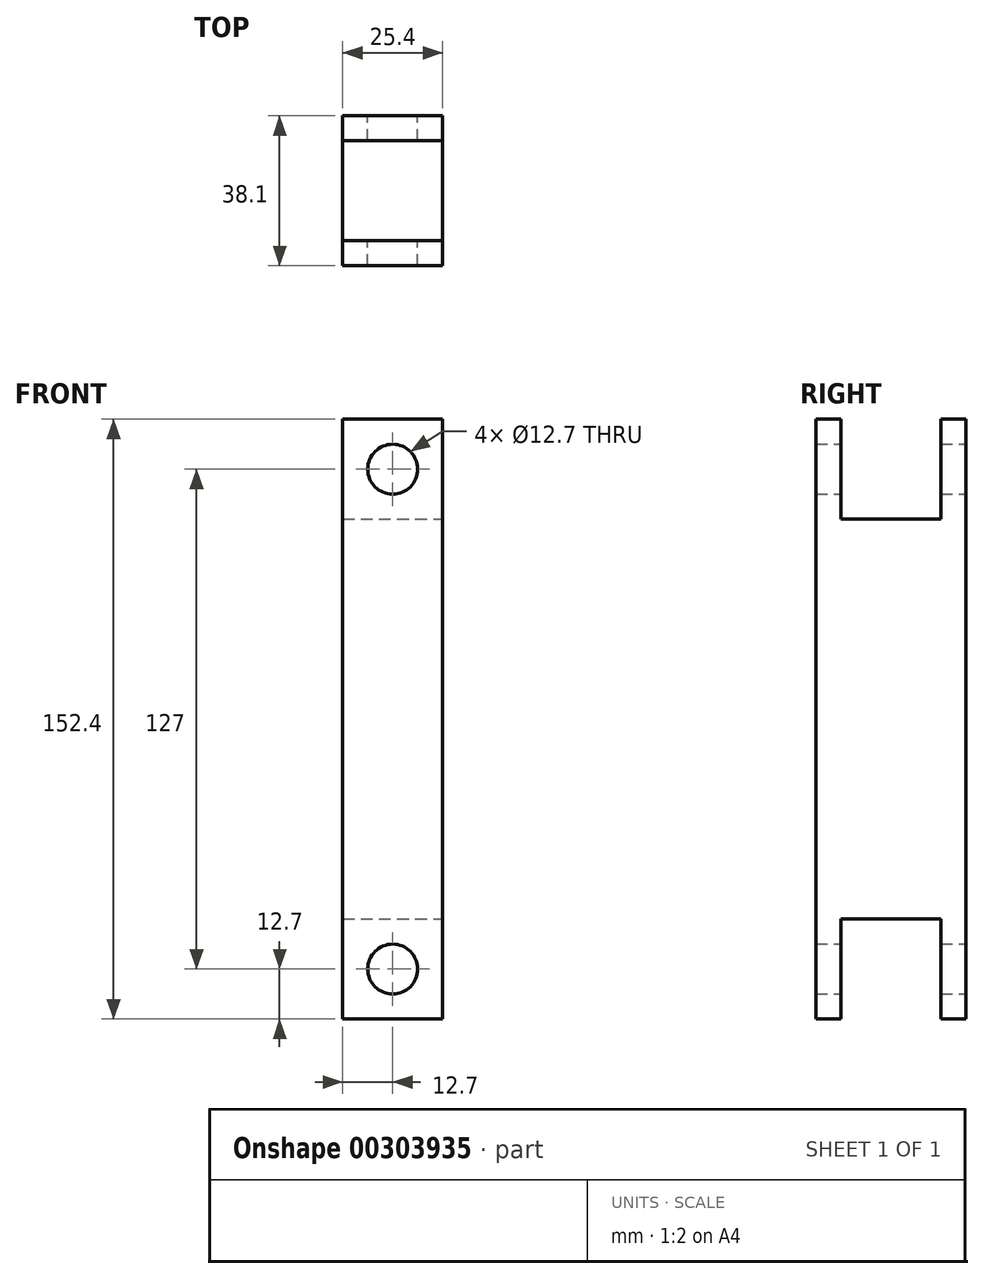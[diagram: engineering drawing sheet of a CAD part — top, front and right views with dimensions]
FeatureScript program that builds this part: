
annotation { "Feature Type Name" : "Feature", "Feature Type Description" : "" }
export const myFeature = defineFeature(function(context is Context, id is Id, definition is map)
    precondition{}
    {
        {
            var Q0;
            Q0=qCreatedBy(makeId("Front.planeOp"),FACE);
            var sketch = newSketch(context, id + "F0", { "sketchPlane" : qUnion([Q0])});
            skCircle(sketch, "E0", {"center": v(0, 0) * mm, "radius": 12.7 * mm});
            skCircle(sketch, "E1", {"center": v(0, -127) * mm, "radius": 12.7 * mm});
            skLineSegment(sketch, "E2", {"start": v(12.7, 0) * mm, "end": v(12.7, -127) * mm});
            skLineSegment(sketch, "E3", {"start": v(-12.7, -127) * mm, "end": v(-12.7, 0) * mm});
            skCircle(sketch, "E4", {"center": v(0, -127) * mm, "radius": 6.35 * mm});
            skCircle(sketch, "E5", {"center": v(0, 0) * mm, "radius": 6.35 * mm});
            skLineSegment(sketch, "E6.bottom", {"start": v(12.7, -114.3) * mm, "end": v(-12.7, -114.3) * mm});
            skLineSegment(sketch, "E6.top", {"start": v(12.7, -139.7) * mm, "end": v(-12.7, -139.7) * mm});
            skLineSegment(sketch, "E6.left", {"start": v(12.7, -114.3) * mm, "end": v(12.7, -139.7) * mm});
            skLineSegment(sketch, "E6.right", {"start": v(-12.7, -114.3) * mm, "end": v(-12.7, -139.7) * mm});
            skLineSegment(sketch, "E7.bottom", {"start": v(12.7, -12.7) * mm, "end": v(-12.7, -12.7) * mm});
            skLineSegment(sketch, "E7.top", {"start": v(12.7, 12.7) * mm, "end": v(-12.7, 12.7) * mm});
            skLineSegment(sketch, "E7.left", {"start": v(12.7, -12.7) * mm, "end": v(12.7, 12.7) * mm});
            skLineSegment(sketch, "E7.right", {"start": v(-12.7, -12.7) * mm, "end": v(-12.7, 12.7) * mm});
            skSolve(sketch);
        }
        {
            var Q0;
            Q0 = qSketchRegion(id + "F0", true);
            extrude(context, id + "F1", {"entities" : qUnion([Q0]), "endBound" : BoundingType.SYMMETRIC, "depth" : 38.1 * mm});
        }
        {
            var Q0;
            Q0=qCreatedBy(makeId("Right.planeOp"),FACE);
            var sketch = newSketch(context, id + "F2", { "sketchPlane" : qUnion([Q0])});
            skLineSegment(sketch, "E8.bottom", {"start": v(12.7, 12.7) * mm, "end": v(-12.7, 12.7) * mm});
            skLineSegment(sketch, "E8.top", {"start": v(12.7, -12.7) * mm, "end": v(-12.7, -12.7) * mm});
            skLineSegment(sketch, "E8.left", {"start": v(12.7, 12.7) * mm, "end": v(12.7, -12.7) * mm});
            skLineSegment(sketch, "E8.right", {"start": v(-12.7, 12.7) * mm, "end": v(-12.7, -12.7) * mm});
            skPoint(sketch, "E8.middle", {"position": v(0, 0) * mm});
            skLineSegment(sketch, "E9.bottom", {"start": v(12.7, -114.3) * mm, "end": v(-12.7, -114.3) * mm});
            skLineSegment(sketch, "E9.top", {"start": v(12.7, -139.7) * mm, "end": v(-12.7, -139.7) * mm});
            skLineSegment(sketch, "E9.left", {"start": v(12.7, -114.3) * mm, "end": v(12.7, -139.7) * mm});
            skLineSegment(sketch, "E9.right", {"start": v(-12.7, -114.3) * mm, "end": v(-12.7, -139.7) * mm});
            skPoint(sketch, "E9.middle", {"position": v(0, -127) * mm});
            skSolve(sketch);
        }
        {
            var Q0;
            Q0 = qSketchRegion(id + "F2", true);
            extrude(context, id + "F3", {"entities" : qUnion([Q0]), "operationType" : NewBodyOperationType.REMOVE, "endBound" : BoundingType.SYMMETRIC, "oppositeDirection" : true, "depth" : 50.8 * mm});
        }
    });
